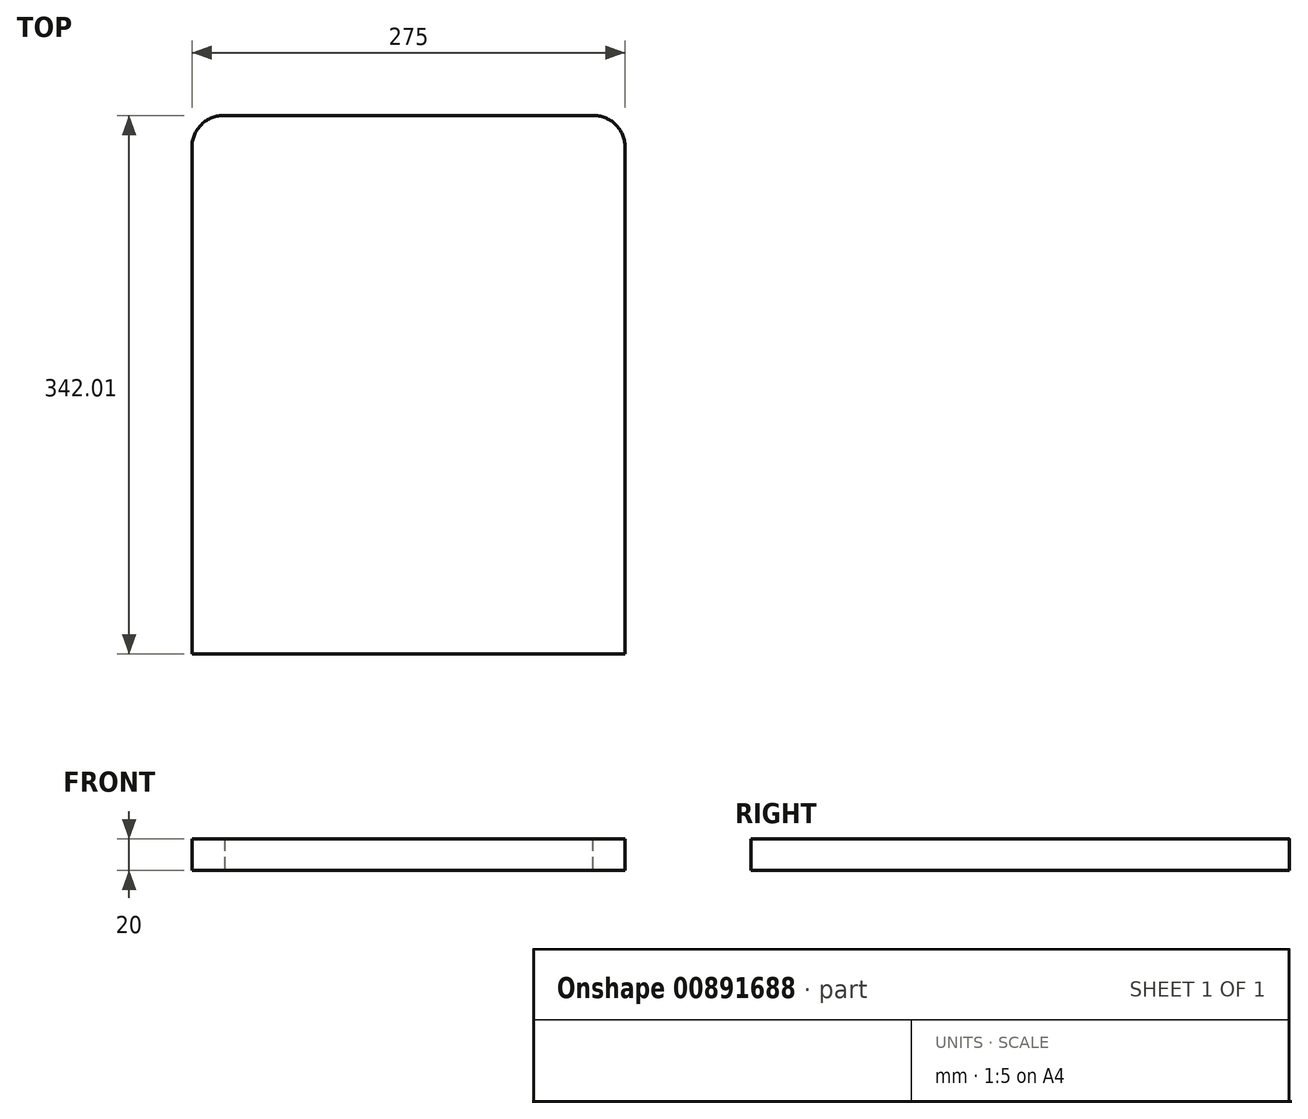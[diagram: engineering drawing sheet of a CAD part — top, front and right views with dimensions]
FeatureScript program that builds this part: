
annotation { "Feature Type Name" : "Feature", "Feature Type Description" : "" }
export const myFeature = defineFeature(function(context is Context, id is Id, definition is map)
    precondition{}
    {
        {
            var Q0;
            Q0=qCreatedBy(makeId("Top.planeOp"),FACE);
            var sketch = newSketch(context, id + "F0", { "sketchPlane" : qUnion([Q0])});
            skFitSpline(sketch, "E0.0.0", {"points": [v(222.24, 427.22) * mm, v(215.5, 429.07) * mm, v(196.44, 434.28) * mm, v(159.63, 464.69) * mm, v(135.76, 484.28) * mm]});
            skArc(sketch, "E0.0.1", {"start": v(135.76, 484.28) * mm, "mid": v(0, 567.46) * mm, "end": v(-135.76, 484.28) * mm});
            skFitSpline(sketch, "E0.0.2", {"points": [v(-135.76, 484.28) * mm, v(-159.63, 464.69) * mm, v(-196.44, 434.28) * mm, v(-215.5, 429.07) * mm, v(-222.24, 427.22) * mm]});
            skArc(sketch, "E0.0.4", {"start": v(-309.42, 390.28) * mm, "mid": v(-312.68, 382.2) * mm, "end": v(-319.87, 377.3) * mm});
            skFitSpline(sketch, "E0.0.5", {"points": [v(-314.05, 379.09) * mm, v(-349.26, 368.46) * mm, v(-392.1, 351.55) * mm, v(-410.06, 337.43) * mm]});
            skEllipticalArc(sketch, "E0.0.6", {});
            skArc(sketch, "E0.0.7", {"start": v(-404.46, 196.44) * mm, "mid": v(-395.87, 191.21) * mm, "end": v(-386.4, 187.8) * mm});
            skFitSpline(sketch, "E0.0.8", {"points": [v(-394.78, 189.9) * mm, v(-344.92, 177.5) * mm, v(-241.75, 151.88) * mm, v(-181.26, 51.75) * mm, v(-150, 0) * mm]});
            skLineSegment(sketch, "E0.0.9", {"start": v(-150, 0) * mm, "end": v(-90, 0) * mm});
            skLineSegment(sketch, "E0.0.10", {"start": v(-90, 0) * mm, "end": v(-90, 110) * mm});
            skArc(sketch, "E0.0.11", {"start": v(-90, 110) * mm, "mid": v(0, 200) * mm, "end": v(90, 110) * mm});
            skLineSegment(sketch, "E0.0.12", {"start": v(90, 110) * mm, "end": v(90, 0) * mm});
            skLineSegment(sketch, "E0.0.13", {"start": v(90, 0) * mm, "end": v(150, 0) * mm});
            skFitSpline(sketch, "E0.0.14", {"points": [v(150, 0) * mm, v(181.26, 51.75) * mm, v(241.75, 151.88) * mm, v(344.92, 177.5) * mm, v(394.78, 189.9) * mm]});
            skArc(sketch, "E0.0.15", {"start": v(386.4, 187.8) * mm, "mid": v(395.87, 191.21) * mm, "end": v(404.46, 196.44) * mm});
            skEllipticalArc(sketch, "E0.0.16", {});
            skFitSpline(sketch, "E0.0.17", {"points": [v(410.06, 337.43) * mm, v(392.1, 351.55) * mm, v(349.26, 368.46) * mm, v(314.05, 379.09) * mm]});
            skLineSegment(sketch, "E1.0", {"start": v(-240.1, 290) * mm, "end": v(-178.5, 290) * mm});
            skLineSegment(sketch, "E1.1", {"start": v(-178.5, 290) * mm, "end": v(-178.5, 325.2) * mm});
            skLineSegment(sketch, "E1.2", {"start": v(-178.5, 325.2) * mm, "end": v(-240.1, 325.2) * mm});
            skLineSegment(sketch, "E1.3", {"start": v(-240.1, 290) * mm, "end": v(-240.1, 325.2) * mm});
            skLineSegment(sketch, "E1.4", {"start": v(-250.1, 290) * mm, "end": v(-250.1, 325.2) * mm});
            skLineSegment(sketch, "E1.5", {"start": v(-250.1, 325.2) * mm, "end": v(-311.7, 325.2) * mm});
            skLineSegment(sketch, "E1.6", {"start": v(-311.7, 290) * mm, "end": v(-250.1, 290) * mm});
            skLineSegment(sketch, "E1.7", {"start": v(-311.7, 290) * mm, "end": v(-311.7, 325.2) * mm});
            skLineSegment(sketch, "E2.0", {"start": v(-383.3, 290) * mm, "end": v(-321.7, 290) * mm});
            skLineSegment(sketch, "E3.0", {"start": v(-321.7, 325.2) * mm, "end": v(-383.3, 325.2) * mm});
            skLineSegment(sketch, "E4.0", {"start": v(-321.7, 290) * mm, "end": v(-321.7, 325.2) * mm});
            skLineSegment(sketch, "E5.0", {"start": v(-383.3, 290) * mm, "end": v(-383.3, 325.2) * mm});
            skFitSpline(sketch, "E6.0", {"points": [v(-342.67, 339.28) * mm, v(-317.97, 353.62) * mm, v(-277.69, 364.45) * mm, v(-252.88, 405.7) * mm, v(-252.65, 405.6) * mm, v(-252.66, 408.6) * mm]});
            skArc(sketch, "E7.0", {"start": v(-250.27, 406.87) * mm, "mid": v(-251.77, 407.17) * mm, "end": v(-252.75, 406) * mm});
            skFitSpline(sketch, "E8.0", {"points": [v(-250.27, 406.87) * mm, v(-244.43, 403.08) * mm, v(-228.6, 392.87) * mm, v(-192.33, 407.72) * mm, v(-169.18, 417.08) * mm]});
            skArc(sketch, "E9.0", {"start": v(-169.05, 414.28) * mm, "mid": v(-169.97, 415.86) * mm, "end": v(-171.8, 416.02) * mm});
            skArc(sketch, "E10.0", {"start": v(-332.8, 344.66) * mm, "mid": v(-334, 342.02) * mm, "end": v(-331.71, 340.22) * mm});
            skArc(sketch, "E11.0.0", {"start": v(367.9, 246.89) * mm, "mid": v(366.57, 245.65) * mm, "end": v(366.79, 243.85) * mm});
            skArc(sketch, "E11.0.1", {"start": v(366.79, 243.85) * mm, "mid": v(401.04, 245.6) * mm, "end": v(383.39, 275) * mm});
            skLineSegment(sketch, "E11.0.2", {"start": v(383.39, 275) * mm, "end": v(-383.39, 275) * mm});
            skArc(sketch, "E11.0.3", {"start": v(-383.39, 275) * mm, "mid": v(-401.04, 245.6) * mm, "end": v(-366.79, 243.85) * mm});
            skArc(sketch, "E11.0.4", {"start": v(-366.79, 243.85) * mm, "mid": v(-366.57, 245.65) * mm, "end": v(-367.9, 246.89) * mm});
            skEllipticalArc(sketch, "E11.0.5", {});
            skArc(sketch, "E11.0.6", {"start": v(-369.23, 261.25) * mm, "mid": v(-358.46, 257.25) * mm, "end": v(-353.55, 246.86) * mm});
            skArc(sketch, "E11.0.7", {"start": v(-353.55, 246.86) * mm, "mid": v(-353.08, 242.95) * mm, "end": v(-352.1, 239.13) * mm});
            skFitSpline(sketch, "E11.0.8", {"points": [v(-353.7, 243.85) * mm, v(-350.61, 235.19) * mm, v(-342.3, 200.93) * mm, v(-287.54, 161.27) * mm, v(-255.18, 135.34) * mm]});
            skFitSpline(sketch, "E11.0.9", {"points": [v(-394.78, 189.9) * mm, v(-344.92, 177.5) * mm, v(-241.75, 151.88) * mm, v(-181.26, 51.75) * mm, v(-150, 0) * mm]});
            skFitSpline(sketch, "E11.0.15", {"points": [v(150, 0) * mm, v(181.26, 51.75) * mm, v(241.75, 151.88) * mm, v(344.92, 177.5) * mm, v(394.78, 189.9) * mm]});
            skFitSpline(sketch, "E11.0.16", {"points": [v(255.18, 135.34) * mm, v(287.54, 161.27) * mm, v(342.3, 200.93) * mm, v(350.61, 235.19) * mm, v(353.7, 243.85) * mm]});
            skArc(sketch, "E11.0.17", {"start": v(352.1, 239.13) * mm, "mid": v(353.08, 242.95) * mm, "end": v(353.55, 246.86) * mm});
            skArc(sketch, "E11.0.18", {"start": v(353.55, 246.86) * mm, "mid": v(358.46, 257.25) * mm, "end": v(369.23, 261.25) * mm});
            skEllipticalArc(sketch, "E11.0.19", {});
            skLineSegment(sketch, "E12.0.0", {"start": v(305.94, 275) * mm, "end": v(-305.94, 275) * mm});
            skArc(sketch, "E12.0.1", {"start": v(-305.94, 275) * mm, "mid": v(-327.36, 237.1) * mm, "end": v(-283.84, 238.31) * mm});
            skArc(sketch, "E12.0.2", {"start": v(-283.84, 238.31) * mm, "mid": v(-283.78, 240.06) * mm, "end": v(-285.12, 241.19) * mm});
            skEllipticalArc(sketch, "E12.0.3", {});
            skFitSpline(sketch, "E12.0.4", {"points": [v(-286.27, 259.2) * mm, v(1000, -265.74) * mm, v(256.47, 1000) * mm]});
            skFitSpline(sketch, "E12.0.5", {"points": [v(-285.63, 259.1) * mm, v(1000, -265.14) * mm, v(258.09, 1000) * mm]});
            skFitSpline(sketch, "E12.0.6", {"points": [v(-265.5, 243.26) * mm, v(-263.97, 221.32) * mm, v(-260.75, 173.86) * mm, v(-230.38, 123.02) * mm, v(-214.22, 95.6) * mm]});
            skFitSpline(sketch, "E12.0.7", {"points": [v(-394.78, 189.9) * mm, v(-344.92, 177.5) * mm, v(-241.75, 151.88) * mm, v(-181.26, 51.75) * mm, v(-150, 0) * mm]});
            skFitSpline(sketch, "E12.0.13", {"points": [v(150, 0) * mm, v(181.26, 51.75) * mm, v(241.75, 151.88) * mm, v(344.92, 177.5) * mm, v(394.78, 189.9) * mm]});
            skFitSpline(sketch, "E12.0.14", {"points": [v(214.22, 95.6) * mm, v(230.38, 123.02) * mm, v(260.75, 173.86) * mm, v(263.97, 221.32) * mm, v(265.5, 243.26) * mm]});
            skFitSpline(sketch, "E12.0.15", {"points": [v(265.14, 238.31) * mm, v(1000, 265.14) * mm, v(258.09, 1000) * mm]});
            skLineSegment(sketch, "E12.0.16", {"start": v(285.63, 259.1) * mm, "end": v(286.27, 259.2) * mm});
            skEllipticalArc(sketch, "E12.0.17", {});
            skArc(sketch, "E12.0.18", {"start": v(285.12, 241.19) * mm, "mid": v(283.78, 240.06) * mm, "end": v(283.84, 238.31) * mm});
            skArc(sketch, "E12.0.19", {"start": v(283.84, 238.31) * mm, "mid": v(327.36, 237.1) * mm, "end": v(305.94, 275) * mm});
            skArc(sketch, "E13.0.0", {"start": v(188.69, 224.82) * mm, "mid": v(238.32, 232.86) * mm, "end": v(210.88, 275) * mm});
            skLineSegment(sketch, "E13.0.1", {"start": v(210.88, 275) * mm, "end": v(-210.88, 275) * mm});
            skArc(sketch, "E13.0.2", {"start": v(-210.88, 275) * mm, "mid": v(-238.32, 232.86) * mm, "end": v(-188.69, 224.82) * mm});
            skArc(sketch, "E13.0.3", {"start": v(-188.69, 224.82) * mm, "mid": v(-188.58, 226.71) * mm, "end": v(-190.1, 227.85) * mm});
            skEllipticalArc(sketch, "E13.0.4", {});
            skFitSpline(sketch, "E13.0.5", {"points": [v(-190.78, 251.9) * mm, v(1000, -168.95) * mm, v(251.9, 1000) * mm]});
            skArc(sketch, "E13.0.6", {"start": v(-170.52, 233.6) * mm, "mid": v(-170.48, 227.5) * mm, "end": v(-171.67, 221.5) * mm});
            skFitSpline(sketch, "E13.0.7", {"points": [v(-170.36, 225.76) * mm, v(-179.25, 197.05) * mm, v(-199.12, 132.86) * mm, v(-167.48, 47.3) * mm, v(-150, 0) * mm]});
            skFitSpline(sketch, "E13.0.13", {"points": [v(150, 0) * mm, v(167.48, 47.3) * mm, v(199.12, 132.86) * mm, v(179.25, 197.05) * mm, v(170.36, 225.76) * mm]});
            skArc(sketch, "E13.0.14", {"start": v(171.67, 221.5) * mm, "mid": v(170.48, 227.5) * mm, "end": v(170.52, 233.6) * mm});
            skFitSpline(sketch, "E13.0.15", {"points": [v(170.36, 225.76) * mm, v(1000, 168.95) * mm, v(251.9, 1000) * mm]});
            skEllipticalArc(sketch, "E13.0.16", {});
            skArc(sketch, "E13.0.17", {"start": v(190.1, 227.85) * mm, "mid": v(188.58, 226.71) * mm, "end": v(188.69, 224.82) * mm});
            skLineSegment(sketch, "E14", {"start": v(-331.71, 340.22) * mm, "end": v(-198.5, 340.69) * mm});
            skLineSegment(sketch, "E15", {"start": v(-168.92, 340.79) * mm, "end": v(-169.05, 414.28) * mm});
            skFitSpline(sketch, "E16", {"points": [v(-309.42, 390.28) * mm, v(-310.43, 397.88) * mm, v(-313.22, 403.87) * mm, v(-319.74, 407.36) * mm, v(-326.56, 409.03) * mm, v(-336.27, 408.88) * mm, v(-344.6, 406.3) * mm, v(-349.31, 401.45) * mm, v(-350.68, 396.14) * mm, v(-348.1, 390.38) * mm, v(-342.18, 385.98) * mm, v(-349.31, 386.43) * mm, v(-357.3, 391.91) * mm, v(-359.87, 398.89) * mm, v(-360.53, 404.48) * mm, v(-359.92, 410.03) * mm, v(-358.56, 414.95) * mm, v(-355.53, 420.61) * mm, v(-347.6, 428.48) * mm, v(-336.84, 434.93) * mm, v(-325.35, 437.99) * mm, v(-316.06, 437.95) * mm, v(-306.16, 435.7) * mm, v(-299.83, 432.89) * mm, v(-292.54, 427.4) * mm, v(-289.54, 422.08) * mm, v(-289.78, 416.43) * mm, v(-288.99, 413.5) * mm, v(-284.18, 413.54) * mm, v(-277.28, 420.3) * mm, v(-275.39, 426.5) * mm, v(-275.68, 437.35) * mm, v(-274.73, 450.85) * mm, v(-268.87, 462.58) * mm, v(-258.44, 470.61) * mm, v(-245.92, 473.96) * mm, v(-234.58, 474.32) * mm, v(-224.62, 471.95) * mm, v(-219.05, 468.93) * mm, v(-214.82, 465.41) * mm, v(-210.76, 459.35) * mm, v(-210.3, 450.66) * mm, v(-213.6, 444.23) * mm, v(-219.23, 439.08) * mm, v(-223.94, 437.12) * mm, v(-226.82, 436.48) * mm, v(-228.8, 436.84) * mm, v(-227, 438.29) * mm, v(-224.93, 439.28) * mm, v(-222.76, 440.81) * mm, v(-221.4, 443.17) * mm, v(-220.7, 446.77) * mm, v(-221.12, 450.52) * mm, v(-223.7, 453.85) * mm, v(-227.55, 456.2) * mm, v(-231.66, 457.32) * mm, v(-236.43, 457.82) * mm, v(-239.68, 457.23) * mm, v(-243.44, 455.26) * mm, v(-247.03, 451.54) * mm, v(-248.96, 447.62) * mm, v(-249.62, 441.06) * mm, v(-248.82, 436.85) * mm, v(-246.6, 432.46) * mm, v(-243.05, 429.54) * mm, v(-238.25, 427.74) * mm, v(-231.93, 426.7) * mm, v(-225.96, 426.77) * mm, v(-222.24, 427.22) * mm], "startDerivative": vector(-24.65, 493.31) * mm, "endDerivative": vector(305.63, 42.31) * mm});
            skFitSpline(sketch, "E17.MirrorCS", {"points": [v(309.42, 390.28) * mm, v(310.43, 397.88) * mm, v(313.22, 403.87) * mm, v(319.74, 407.36) * mm, v(326.56, 409.03) * mm, v(336.27, 408.88) * mm, v(344.6, 406.3) * mm, v(349.31, 401.45) * mm, v(350.68, 396.14) * mm, v(348.1, 390.38) * mm, v(342.18, 385.98) * mm, v(349.31, 386.43) * mm, v(357.3, 391.91) * mm, v(359.87, 398.89) * mm, v(360.53, 404.48) * mm, v(359.92, 410.03) * mm, v(358.56, 414.95) * mm, v(355.53, 420.61) * mm, v(347.6, 428.48) * mm, v(336.84, 434.93) * mm, v(325.35, 437.99) * mm, v(316.06, 437.95) * mm, v(306.16, 435.7) * mm, v(299.83, 432.89) * mm, v(292.54, 427.4) * mm, v(289.54, 422.08) * mm, v(289.78, 416.43) * mm, v(288.99, 413.5) * mm, v(284.18, 413.54) * mm, v(277.28, 420.3) * mm, v(275.39, 426.5) * mm, v(275.68, 437.35) * mm, v(274.73, 450.85) * mm, v(268.87, 462.58) * mm, v(258.44, 470.61) * mm, v(245.92, 473.96) * mm, v(234.58, 474.32) * mm, v(224.62, 471.95) * mm, v(219.05, 468.93) * mm, v(214.82, 465.41) * mm, v(210.76, 459.35) * mm, v(210.3, 450.66) * mm, v(213.6, 444.23) * mm, v(219.23, 439.08) * mm, v(223.94, 437.12) * mm, v(226.82, 436.48) * mm, v(228.8, 436.84) * mm, v(227, 438.29) * mm, v(224.93, 439.28) * mm, v(222.76, 440.81) * mm, v(221.4, 443.17) * mm, v(220.7, 446.77) * mm, v(221.12, 450.52) * mm, v(223.7, 453.85) * mm, v(227.55, 456.2) * mm, v(231.66, 457.32) * mm, v(236.43, 457.82) * mm, v(239.68, 457.23) * mm, v(243.44, 455.26) * mm, v(247.03, 451.54) * mm, v(248.96, 447.62) * mm, v(249.62, 441.06) * mm, v(248.82, 436.85) * mm, v(246.6, 432.46) * mm, v(243.05, 429.54) * mm, v(238.25, 427.74) * mm, v(231.93, 426.7) * mm, v(225.96, 426.77) * mm, v(222.24, 427.22) * mm], "startDerivative": vector(24.65, 493.31) * mm, "endDerivative": vector(-305.63, 42.31) * mm});
            skFitSpline(sketch, "E18.MirrorCS", {"points": [v(342.67, 339.28) * mm, v(317.97, 353.62) * mm, v(277.69, 364.45) * mm, v(252.88, 405.7) * mm, v(252.65, 405.6) * mm, v(252.66, 408.6) * mm]});
            skFitSpline(sketch, "E19.MirrorCS", {"points": [v(250.27, 406.87) * mm, v(244.43, 403.08) * mm, v(228.6, 392.87) * mm, v(192.33, 407.72) * mm, v(169.18, 417.08) * mm]});
            skLineSegment(sketch, "E20.MirrorCS", {"start": v(168.92, 340.79) * mm, "end": v(169.05, 414.28) * mm});
            skLineSegment(sketch, "E21.MirrorCS", {"start": v(331.71, 340.22) * mm, "end": v(168.92, 340.79) * mm});
            skArc(sketch, "E22.MirrorCS", {"start": v(169.05, 414.28) * mm, "mid": v(169.97, 415.86) * mm, "end": v(171.8, 416.02) * mm});
            skArc(sketch, "E23.MirrorCS", {"start": v(250.27, 406.87) * mm, "mid": v(251.77, 407.17) * mm, "end": v(252.75, 406) * mm});
            skArc(sketch, "E24.MirrorCS", {"start": v(332.8, 344.66) * mm, "mid": v(334, 342.02) * mm, "end": v(331.71, 340.22) * mm});
            skArc(sketch, "E25.MirrorCS", {"start": v(309.42, 390.28) * mm, "mid": v(312.68, 382.2) * mm, "end": v(319.87, 377.3) * mm});
            skFitSpline(sketch, "E26", {"points": [v(-250.27, 406.87) * mm, v(-244.43, 403.08) * mm, v(-228.6, 392.87) * mm, v(-192.33, 407.72) * mm, v(-169.18, 417.08) * mm]});
            skLineSegment(sketch, "E27", {"start": v(-198.5, 340.69) * mm, "end": v(-168.92, 340.79) * mm});
            skPoint(sketch, "E28", {"position": v(0, 275) * mm});
            skLineSegment(sketch, "E29", {"start": v(-178.5, 340.75) * mm, "end": v(-178.5, 413.32) * mm});
            skLineSegment(sketch, "E30.MirrorCS", {"start": v(178.5, 340.75) * mm, "end": v(178.5, 413.32) * mm});
            skLineSegment(sketch, "E31.MirrorCS", {"start": v(178.5, 290) * mm, "end": v(178.5, 325.2) * mm});
            skLineSegment(sketch, "E32.MirrorCS", {"start": v(178.5, 325.2) * mm, "end": v(240.1, 325.2) * mm});
            skLineSegment(sketch, "E33.MirrorCS", {"start": v(240.1, 290) * mm, "end": v(178.5, 290) * mm});
            skLineSegment(sketch, "E34.MirrorCS", {"start": v(240.1, 290) * mm, "end": v(240.1, 325.2) * mm});
            skLineSegment(sketch, "E35.MirrorCS", {"start": v(250.1, 290) * mm, "end": v(250.1, 325.2) * mm});
            skLineSegment(sketch, "E36.MirrorCS", {"start": v(250.1, 325.2) * mm, "end": v(311.7, 325.2) * mm});
            skLineSegment(sketch, "E37.MirrorCS", {"start": v(311.7, 290) * mm, "end": v(250.1, 290) * mm});
            skLineSegment(sketch, "E38.MirrorCS", {"start": v(311.7, 290) * mm, "end": v(311.7, 325.2) * mm});
            skLineSegment(sketch, "E39.MirrorCS", {"start": v(321.7, 290) * mm, "end": v(321.7, 325.2) * mm});
            skLineSegment(sketch, "E40.MirrorCS", {"start": v(321.7, 325.2) * mm, "end": v(383.3, 325.2) * mm});
            skLineSegment(sketch, "E41.MirrorCS", {"start": v(383.3, 290) * mm, "end": v(321.7, 290) * mm});
            skLineSegment(sketch, "E42.MirrorCS", {"start": v(383.3, 290) * mm, "end": v(383.3, 325.2) * mm});
            const initialGuessF0  = {"E0.0.6": [-0.34931216680627963, 0.26310522471521947, -0.8795186508433591, 0.4758644164241295, 0.09801349999999999, 0.086147, 5.8461119226871325, 1.3987543209554119], "E0.0.16": [0.34931216680627963, 0.26310522471521947, 0.8795186508433591, 0.4758644164241295, 0.09801349999999999, 0.086147, 4.884430986224174, 0.4370733844924535], "E11.0.5": [-0.3692299729374505, 0.25402610760164496, -1, 0, 0.00868, 0.0072229875998473525, 4.71238898038469, 1.7242785659408997], "E11.0.19": [0.3692299729374472, 0.2540261076016343, 1, 0, 0.00868, 0.0072229875998473525, 4.558906741237017, 1.5707963267948966], "E12.0.3": [-0.2862692176634982, 0.25016623719894915, 1, 0, 0.01114790895395411, 0.00902888915716235, 1.5707963267948966, 4.816091749526819], "E12.0.17": [0.28626921761494883, 0.25016623719894915, 1, 0, 0.01114790895395411, 0.00902888915716235, 4.6086862112438105, 1.5707963267948968], "E13.0.4": [-0.19077662931411604, 0.2398668370838165, -1, 0, 0.012873693325351057, 0.012037203490749382, 4.71238898038469, 1.6233236227230905], "E13.0.16": [0.19077662931381673, 0.2398668370838165, -1, 0, 0.012873693325351057, 0.012037203490749382, 1.5182690308667026, 4.71238898038469]};
            skSetInitialGuess(sketch, initialGuessF0);
            skSolve(sketch);
        }
        {
            var Q0;
            Q0=qCreatedBy(makeId("Top.planeOp"),FACE);
            var sketch = newSketch(context, id + "F1", { "sketchPlane" : qUnion([Q0])});
            skArc(sketch, "E43.0.0", {"start": v(119.38, 608.82) * mm, "mid": v(127.8, 607.3) * mm, "end": v(129.32, 598.88) * mm});
            skArc(sketch, "E43.0.1", {"start": v(129.32, 598.88) * mm, "mid": v(127.96, 594.8) * mm, "end": v(127.5, 590.54) * mm});
            skLineSegment(sketch, "E43.0.2", {"start": v(127.5, 590.54) * mm, "end": v(127.5, 457) * mm});
            skFitSpline(sketch, "E43.0.5", {"points": [v(146.5, 457) * mm, v(149.6, 481.12) * mm, v(148.09, 514.33) * mm, v(141.97, 555.55) * mm, v(150.87, 577.14) * mm, v(150.08, 584.83) * mm, v(149.2, 590.04) * mm, v(146.76, 595.97) * mm, v(148.7, 602.44) * mm, v(153.43, 607.82) * mm, v(159.2, 620.23) * mm, v(152.22, 634.34) * mm, v(138.51, 640.38) * mm, v(127.66, 637.82) * mm, v(123.75, 632.76) * mm, v(115.5, 631.57) * mm, v(101.19, 632.87) * mm, v(83.98, 643.25) * mm, v(68.12, 650.61) * mm, v(57.61, 655.2) * mm, v(46.5, 657.99) * mm, v(38.39, 655.17) * mm, v(34.33, 652.95) * mm, v(28.58, 651.08) * mm, v(24.82, 655.4) * mm, v(15.24, 664.25) * mm, v(0, 668.44) * mm, v(-15.24, 664.25) * mm, v(-24.82, 655.4) * mm, v(-28.58, 651.08) * mm, v(-34.33, 652.95) * mm, v(-38.39, 655.17) * mm, v(-46.5, 657.99) * mm, v(-57.61, 655.2) * mm, v(-68.12, 650.61) * mm, v(-83.98, 643.25) * mm, v(-101.19, 632.87) * mm, v(-115.5, 631.57) * mm, v(-123.75, 632.76) * mm, v(-127.66, 637.82) * mm, v(-138.51, 640.38) * mm, v(-152.22, 634.34) * mm, v(-159.2, 620.23) * mm, v(-153.43, 607.82) * mm, v(-148.7, 602.44) * mm, v(-146.76, 595.97) * mm, v(-149.2, 590.04) * mm, v(-150.08, 584.83) * mm, v(-150.87, 577.14) * mm, v(-141.97, 555.55) * mm, v(-148.09, 514.33) * mm, v(-149.6, 481.12) * mm, v(-146.5, 457) * mm]});
            skLineSegment(sketch, "E43.0.8", {"start": v(-127.5, 457) * mm, "end": v(-127.5, 590.54) * mm});
            skArc(sketch, "E43.0.9", {"start": v(-127.5, 590.54) * mm, "mid": v(-127.96, 594.8) * mm, "end": v(-129.32, 598.88) * mm});
            skArc(sketch, "E43.0.10", {"start": v(-129.32, 598.88) * mm, "mid": v(-127.8, 607.3) * mm, "end": v(-119.38, 608.82) * mm});
            skArc(sketch, "E43.0.11", {"start": v(-119.38, 608.82) * mm, "mid": v(-115.3, 607.46) * mm, "end": v(-111.04, 607) * mm});
            skLineSegment(sketch, "E43.0.12", {"start": v(-111.04, 607) * mm, "end": v(111.04, 607) * mm});
            skArc(sketch, "E43.0.13", {"start": v(111.04, 607) * mm, "mid": v(115.3, 607.46) * mm, "end": v(119.38, 608.82) * mm});
            skLineSegment(sketch, "E44.0.0", {"start": v(117.5, 597) * mm, "end": v(117.5, 457) * mm});
            skLineSegment(sketch, "E44.0.2", {"start": v(127.5, 457) * mm, "end": v(127.5, 596.4) * mm});
            skArc(sketch, "E44.0.3", {"start": v(127.5, 596.4) * mm, "mid": v(127.8, 607.3) * mm, "end": v(116.9, 607) * mm});
            skLineSegment(sketch, "E44.0.4", {"start": v(116.9, 607) * mm, "end": v(-116.9, 607) * mm});
            skArc(sketch, "E44.0.5", {"start": v(-116.9, 607) * mm, "mid": v(-127.8, 607.3) * mm, "end": v(-127.5, 596.4) * mm});
            skLineSegment(sketch, "E44.0.6", {"start": v(-127.5, 596.4) * mm, "end": v(-127.5, 457) * mm});
            skLineSegment(sketch, "E44.0.8", {"start": v(-117.5, 457) * mm, "end": v(-117.5, 597) * mm});
            skLineSegment(sketch, "E44.0.9", {"start": v(-117.5, 597) * mm, "end": v(117.5, 597) * mm});
            skLineSegment(sketch, "E45.0.0", {"start": v(107.5, 587) * mm, "end": v(107.5, 457) * mm});
            skLineSegment(sketch, "E45.0.2", {"start": v(117.5, 457) * mm, "end": v(117.5, 597) * mm});
            skLineSegment(sketch, "E45.0.3", {"start": v(117.5, 597) * mm, "end": v(-117.5, 597) * mm});
            skLineSegment(sketch, "E45.0.4", {"start": v(-117.5, 597) * mm, "end": v(-117.5, 457) * mm});
            skLineSegment(sketch, "E45.0.6", {"start": v(-107.5, 457) * mm, "end": v(-107.5, 587) * mm});
            skLineSegment(sketch, "E45.0.7", {"start": v(-107.5, 587) * mm, "end": v(107.5, 587) * mm});
            skLineSegment(sketch, "E46", {"start": v(-146.5, 457) * mm, "end": v(146.5, 457) * mm});
            skPoint(sketch, "E43.0.3.end.orphan", {"position": v(146.5, 447) * mm});
            skPoint(sketch, "E47.orphan", {"position": v(117.5, 447) * mm});
            skPoint(sketch, "E48.orphan", {"position": v(127.5, 447) * mm});
            skPoint(sketch, "E49.orphan", {"position": v(107.5, 447) * mm});
            skPoint(sketch, "E50.orphan", {"position": v(-117.5, 447) * mm});
            skPoint(sketch, "E43.0.7.end.orphan", {"position": v(-127.5, 447) * mm});
            skArc(sketch, "E51.MirrorCS", {"start": v(129.32, 315.12) * mm, "mid": v(127.96, 319.2) * mm, "end": v(127.5, 323.46) * mm});
            skArc(sketch, "E52.MirrorCS", {"start": v(111.04, 307) * mm, "mid": v(115.3, 306.54) * mm, "end": v(119.38, 305.18) * mm});
            skArc(sketch, "E53.MirrorCS", {"start": v(127.5, 317.6) * mm, "mid": v(127.8, 306.7) * mm, "end": v(116.9, 307) * mm});
            skArc(sketch, "E54.MirrorCS", {"start": v(-116.9, 307) * mm, "mid": v(-127.8, 306.7) * mm, "end": v(-127.5, 317.6) * mm});
            skArc(sketch, "E55.MirrorCS", {"start": v(119.38, 305.18) * mm, "mid": v(127.8, 306.7) * mm, "end": v(129.32, 315.12) * mm});
            skArc(sketch, "E56.MirrorCS", {"start": v(-119.38, 305.18) * mm, "mid": v(-115.3, 306.54) * mm, "end": v(-111.04, 307) * mm});
            skArc(sketch, "E57.MirrorCS", {"start": v(-129.32, 315.12) * mm, "mid": v(-127.8, 306.7) * mm, "end": v(-119.38, 305.18) * mm});
            skArc(sketch, "E58.MirrorCS", {"start": v(-127.5, 323.46) * mm, "mid": v(-127.96, 319.2) * mm, "end": v(-129.32, 315.12) * mm});
            skLineSegment(sketch, "E59.MirrorCS", {"start": v(127.5, 323.46) * mm, "end": v(127.5, 457) * mm});
            skLineSegment(sketch, "E60.MirrorCS", {"start": v(-111.04, 307) * mm, "end": v(111.04, 307) * mm});
            skPoint(sketch, "E61.MirrorP", {"position": v(117.5, 467) * mm});
            skLineSegment(sketch, "E62.MirrorCS", {"start": v(-127.5, 457) * mm, "end": v(-127.5, 323.46) * mm});
            skLineSegment(sketch, "E63.MirrorCS", {"start": v(-117.5, 317) * mm, "end": v(-117.5, 457) * mm});
            skLineSegment(sketch, "E64.MirrorCS", {"start": v(117.5, 317) * mm, "end": v(-117.5, 317) * mm});
            skPoint(sketch, "E65.MirrorP", {"position": v(127.5, 467) * mm});
            skLineSegment(sketch, "E66.MirrorCS", {"start": v(117.5, 457) * mm, "end": v(117.5, 317) * mm});
            skPoint(sketch, "E67.MirrorP", {"position": v(107.5, 467) * mm});
            skPoint(sketch, "E68.MirrorP", {"position": v(146.5, 467) * mm});
            skLineSegment(sketch, "E69.MirrorCS", {"start": v(-107.5, 327) * mm, "end": v(107.5, 327) * mm});
            skPoint(sketch, "E70.MirrorP", {"position": v(-117.5, 467) * mm});
            skLineSegment(sketch, "E71.MirrorCS", {"start": v(127.5, 457) * mm, "end": v(127.5, 317.6) * mm});
            skPoint(sketch, "E72.MirrorP", {"position": v(-127.5, 467) * mm});
            skLineSegment(sketch, "E73.MirrorCS", {"start": v(-117.5, 457) * mm, "end": v(-117.5, 317) * mm});
            skLineSegment(sketch, "E74.MirrorCS", {"start": v(107.5, 327) * mm, "end": v(107.5, 457) * mm});
            skLineSegment(sketch, "E75.MirrorCS", {"start": v(-127.5, 317.6) * mm, "end": v(-127.5, 457) * mm});
            skLineSegment(sketch, "E76.MirrorCS", {"start": v(-107.5, 457) * mm, "end": v(-107.5, 327) * mm});
            skFitSpline(sketch, "E77.MirrorCS", {"points": [v(146.5, 457) * mm, v(149.6, 432.88) * mm, v(148.09, 399.67) * mm, v(141.97, 358.45) * mm, v(150.87, 336.86) * mm, v(150.08, 329.17) * mm, v(149.2, 323.96) * mm, v(146.76, 318.03) * mm, v(148.7, 311.56) * mm, v(153.43, 306.18) * mm, v(159.2, 293.77) * mm, v(152.22, 279.66) * mm, v(138.51, 273.62) * mm, v(127.66, 276.18) * mm, v(123.75, 281.24) * mm, v(115.5, 282.43) * mm, v(101.19, 281.13) * mm, v(83.98, 270.75) * mm, v(68.12, 263.39) * mm, v(57.61, 258.8) * mm, v(46.5, 256.01) * mm, v(38.39, 258.83) * mm, v(34.33, 261.05) * mm, v(28.58, 262.92) * mm, v(24.82, 258.6) * mm, v(15.24, 249.75) * mm, v(0, 245.56) * mm, v(-15.24, 249.75) * mm, v(-24.82, 258.6) * mm, v(-28.58, 262.92) * mm, v(-34.33, 261.05) * mm, v(-38.39, 258.83) * mm, v(-46.5, 256.01) * mm, v(-57.61, 258.8) * mm, v(-68.12, 263.39) * mm, v(-83.98, 270.75) * mm, v(-101.19, 281.13) * mm, v(-115.5, 282.43) * mm, v(-123.75, 281.24) * mm, v(-127.66, 276.18) * mm, v(-138.51, 273.62) * mm, v(-152.22, 279.66) * mm, v(-159.2, 293.77) * mm, v(-153.43, 306.18) * mm, v(-148.7, 311.56) * mm, v(-146.76, 318.03) * mm, v(-149.2, 323.96) * mm, v(-150.08, 329.17) * mm, v(-150.87, 336.86) * mm, v(-141.97, 358.45) * mm, v(-148.09, 399.67) * mm, v(-149.6, 432.88) * mm, v(-146.5, 457) * mm]});
            skLineSegment(sketch, "E78.MirrorCS", {"start": v(116.9, 307) * mm, "end": v(-116.9, 307) * mm});
            skLineSegment(sketch, "E79.MirrorCS", {"start": v(117.5, 317) * mm, "end": v(117.5, 457) * mm});
            skLineSegment(sketch, "E80.MirrorCS", {"start": v(-117.5, 317) * mm, "end": v(117.5, 317) * mm});
            skLineSegment(sketch, "E81.0", {"start": v(-138, 275) * mm, "end": v(138, 275) * mm});
            skFitSpline(sketch, "E82.trimOffspring", {"points": [v(146.5, 457) * mm, v(149.6, 432.88) * mm, v(148.09, 399.67) * mm, v(141.97, 358.45) * mm, v(150.87, 336.86) * mm, v(150.08, 329.17) * mm, v(149.2, 323.96) * mm, v(146.76, 318.03) * mm, v(148.7, 311.56) * mm, v(153.43, 306.18) * mm, v(159.2, 293.77) * mm, v(152.22, 279.66) * mm, v(138.51, 273.62) * mm, v(127.66, 276.18) * mm, v(123.75, 281.24) * mm, v(115.5, 282.43) * mm, v(101.19, 281.13) * mm, v(83.98, 270.75) * mm, v(68.12, 263.39) * mm, v(57.61, 258.8) * mm, v(46.5, 256.01) * mm, v(38.39, 258.83) * mm, v(34.33, 261.05) * mm, v(28.58, 262.92) * mm, v(24.82, 258.6) * mm, v(15.24, 249.75) * mm, v(0, 245.56) * mm, v(-15.24, 249.75) * mm, v(-24.82, 258.6) * mm, v(-28.58, 262.92) * mm, v(-34.33, 261.05) * mm, v(-38.39, 258.83) * mm, v(-46.5, 256.01) * mm, v(-57.61, 258.8) * mm, v(-68.12, 263.39) * mm, v(-83.98, 270.75) * mm, v(-101.19, 281.13) * mm, v(-115.5, 282.43) * mm, v(-123.75, 281.24) * mm, v(-127.66, 276.18) * mm, v(-138.51, 273.62) * mm, v(-152.22, 279.66) * mm, v(-159.2, 293.77) * mm, v(-153.43, 306.18) * mm, v(-148.7, 311.56) * mm, v(-146.76, 318.03) * mm, v(-149.2, 323.96) * mm, v(-150.08, 329.17) * mm, v(-150.87, 336.86) * mm, v(-141.97, 358.45) * mm, v(-148.09, 399.67) * mm, v(-149.6, 432.88) * mm, v(-146.5, 457) * mm]});
            skPoint(sketch, "E83", {"position": v(0, 275) * mm});
            skPoint(sketch, "E84", {"position": v(0, 667) * mm});
            skSolve(sketch);
        }
        {
            var Q0;
            Q0=qCreatedBy(makeId("Top.planeOp"),FACE);
            var sketch = newSketch(context, id + "F2", { "sketchPlane" : qUnion([Q0])});
            skLineSegment(sketch, "E85.0", {"start": v(116.9, 607) * mm, "end": v(-116.9, 607) * mm});
            skLineSegment(sketch, "E86.0", {"start": v(-127.5, 596.4) * mm, "end": v(-127.5, 457) * mm});
            skLineSegment(sketch, "E87.0", {"start": v(-127.5, 457) * mm, "end": v(-127.5, 323.46) * mm});
            skLineSegment(sketch, "E88.0", {"start": v(127.5, 323.46) * mm, "end": v(127.5, 457) * mm});
            skLineSegment(sketch, "E89.0", {"start": v(127.5, 457) * mm, "end": v(127.5, 596.4) * mm});
            skLineSegment(sketch, "E90.0", {"start": v(116.9, 617) * mm, "end": v(-116.9, 617) * mm});
            skLineSegment(sketch, "E91.0", {"start": v(-137.5, 597) * mm, "end": v(-137.5, 457) * mm});
            skLineSegment(sketch, "E92.0", {"start": v(-137.5, 457) * mm, "end": v(-137.5, 275) * mm});
            skLineSegment(sketch, "E93.0", {"start": v(137.5, 275) * mm, "end": v(137.5, 457) * mm});
            skLineSegment(sketch, "E94.0", {"start": v(137.5, 457) * mm, "end": v(137.5, 597) * mm});
            skArc(sketch, "E95", {"start": v(-116.9, 617) * mm, "mid": v(-131.43, 611.36) * mm, "end": v(-137.5, 597) * mm});
            skArc(sketch, "E96", {"start": v(137.5, 597) * mm, "mid": v(131.43, 611.36) * mm, "end": v(116.9, 617) * mm});
            skLineSegment(sketch, "E97.0", {"start": v(137.5, 275) * mm, "end": v(-137.5, 275) * mm});
            skPoint(sketch, "E98.orphan", {"position": v(-305.94, 275) * mm});
            skPoint(sketch, "E99.orphan", {"position": v(305.94, 275) * mm});
            skSolve(sketch);
        }
        {
            var Q0;
            Q0=makeQuery(id+"F2.imprint","IMPRINT",FACE,{"disambiguationData":[TD([[makeQuery(id+"F2.imprint","IMPRINT",EDGE,{"derivedFrom":sQuery(id+"F2.wireOp",EDGE,"E90.0")}),1.0]])]});
            extrude(context, id + "F3", {"entities" : qUnion([Q0]), "depth" : 20 * mm, "offsetDistance" : 25 * mm});
        }
        {
            var Q0;
            Q0=makeQuery(id+"F3.opExtrude","CAP_FACE",FACE,{"disambiguationData":[OSD([sQuery(id+"F2.wireOp",EDGE,"E90.0"),sQuery(id+"F2.wireOp",EDGE,"E91.0"),sQuery(id+"F2.wireOp",EDGE,"E92.0"),sQuery(id+"F2.wireOp",EDGE,"E93.0"),sQuery(id+"F2.wireOp",EDGE,"E94.0"),sQuery(id+"F2.wireOp",EDGE,"E95"),sQuery(id+"F2.wireOp",EDGE,"E96"),sQuery(id+"F2.wireOp",EDGE,"E97.0")])],"isStart":false});
            cPlane(context, id + "F4", {"entities" : qUnion([Q0]), "cplaneType" : CPlaneType.OFFSET, "offset" : 50 * mm, "width" : 150 * mm, "height" : 150 * mm});
        }
    });
